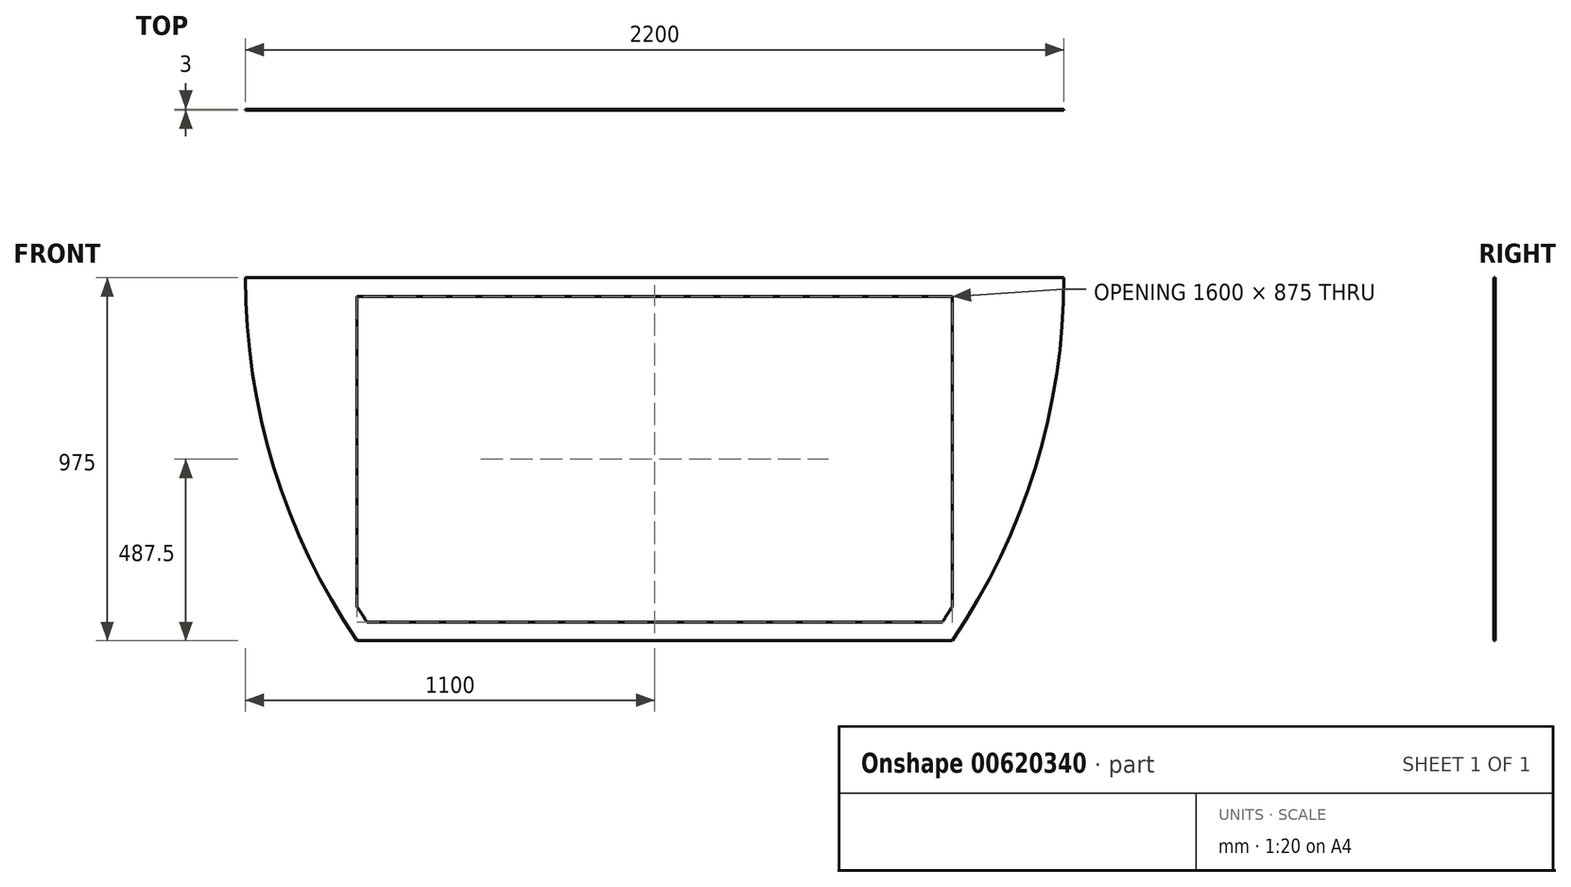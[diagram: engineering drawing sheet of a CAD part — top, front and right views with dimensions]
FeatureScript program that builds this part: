
annotation { "Feature Type Name" : "Feature", "Feature Type Description" : "" }
export const myFeature = defineFeature(function(context is Context, id is Id, definition is map)
    precondition{}
    {
        {
            var Q0;
            Q0=qCreatedBy(makeId("Front.planeOp"),FACE);
            var sketch = newSketch(context, id + "F0", { "sketchPlane" : qUnion([Q0])});
            skLineSegment(sketch, "E0.bottom", {"start": v(-800, 1950) * mm, "end": v(800, 1950) * mm});
            skLineSegment(sketch, "E0.top", {"start": v(-800, 0) * mm, "end": v(800, 0) * mm});
            skLineSegment(sketch, "E0.left", {"start": v(-800, 1950) * mm, "end": v(-800, 0) * mm});
            skLineSegment(sketch, "E0.right", {"start": v(800, 1950) * mm, "end": v(800, 0) * mm});
            skArc(sketch, "E1", {"start": v(800, 0) * mm, "mid": v(1100, 975) * mm, "end": v(800, 1950) * mm});
            skArc(sketch, "E2", {"start": v(-800, 1950) * mm, "mid": v(-1100, 975) * mm, "end": v(-800, 0) * mm});
            skArc(sketch, "E3", {"start": v(-804.9, 1850) * mm, "mid": v(-1049.74, 945.42) * mm, "end": v(-773.28, 50) * mm});
            skArc(sketch, "E4", {"start": v(773.28, 50) * mm, "mid": v(1049.74, 945.42) * mm, "end": v(804.9, 1850) * mm});
            skLineSegment(sketch, "E5", {"start": v(-1050, 975) * mm, "end": v(1050, 975) * mm});
            skPoint(sketch, "E5.startSnap0", {"position": v(-1100, 975) * mm});
            skLineSegment(sketch, "E6", {"start": v(-804.9, 1850) * mm, "end": v(804.9, 1850) * mm});
            skLineSegment(sketch, "E7", {"start": v(-773.28, 50) * mm, "end": v(773.28, 50) * mm});
            skLineSegment(sketch, "E8", {"start": v(0, 1950) * mm, "end": v(0, 975) * mm});
            skLineSegment(sketch, "E9", {"start": v(-25, 1850) * mm, "end": v(-25, 975) * mm});
            skLineSegment(sketch, "E10", {"start": v(-25, 975) * mm, "end": v(25, 975) * mm});
            skLineSegment(sketch, "E11", {"start": v(25, 975) * mm, "end": v(25, 1850) * mm});
            skLineSegment(sketch, "E12", {"start": v(-1099.28, 925) * mm, "end": v(1099.28, 925) * mm});
            skLineSegment(sketch, "E13", {"start": v(-25, 975) * mm, "end": v(-25, 925) * mm});
            skLineSegment(sketch, "E14", {"start": v(25, 975) * mm, "end": v(25, 925) * mm});
            skLineSegment(sketch, "E15", {"start": v(-750, 0) * mm, "end": v(-750, 50) * mm});
            skLineSegment(sketch, "E16", {"start": v(-750, 50) * mm, "end": v(-650, 50) * mm});
            skLineSegment(sketch, "E17", {"start": v(-650, 50) * mm, "end": v(-650, 0) * mm});
            skLineSegment(sketch, "E18", {"start": v(-50, 0) * mm, "end": v(-50, 50) * mm});
            skLineSegment(sketch, "E19", {"start": v(-50, 50) * mm, "end": v(50, 50) * mm});
            skLineSegment(sketch, "E20", {"start": v(50, 50) * mm, "end": v(50, 0) * mm});
            skLineSegment(sketch, "E21", {"start": v(650, 0) * mm, "end": v(650, 50) * mm});
            skLineSegment(sketch, "E22", {"start": v(650, 50) * mm, "end": v(750, 50) * mm});
            skLineSegment(sketch, "E23", {"start": v(750, 50) * mm, "end": v(750, 0) * mm});
            skLineSegment(sketch, "E24", {"start": v(0, 50) * mm, "end": v(0, 0) * mm});
            skLineSegment(sketch, "E25", {"start": v(-800, 1900) * mm, "end": v(800, 1900) * mm});
            skLineSegment(sketch, "E26", {"start": v(-1050, 975) * mm, "end": v(-1100, 975) * mm});
            skLineSegment(sketch, "E27", {"start": v(1050, 975) * mm, "end": v(1100, 975) * mm});
            skSolve(sketch);
        }
        {
            var Q0;
            {var subQ3=sQuery(id+"F0.wireOp",EDGE,"E15");Q0=makeQuery(id+"F0.imprint","IMPRINT",FACE,{"disambiguationData":[TD([[makeQuery(id+"F0.imprint","IMPRINT",EDGE,{"derivedFrom":subQ3}),1.0]])]});}
            var Q1;
            {var subQ0=sQuery(id+"F0.wireOp",EDGE,"E15");Q1=makeQuery(id+"F0.imprint","IMPRINT",FACE,{"disambiguationData":[TD([[makeQuery(id+"F0.imprint","IMPRINT",EDGE,{"derivedFrom":subQ0}),-1.0]])]});}
            var Q2;
            {var subQ0=sQuery(id+"F0.wireOp",EDGE,"E17");Q2=makeQuery(id+"F0.imprint","IMPRINT",FACE,{"disambiguationData":[TD([[makeQuery(id+"F0.imprint","IMPRINT",EDGE,{"derivedFrom":subQ0}),1.0]])]});}
            var Q3;
            {var subQ0=sQuery(id+"F0.wireOp",EDGE,"E18");Q3=makeQuery(id+"F0.imprint","IMPRINT",FACE,{"disambiguationData":[TD([[makeQuery(id+"F0.imprint","IMPRINT",EDGE,{"derivedFrom":subQ0}),-1.0]])]});}
            var Q4;
            {var subQ0=sQuery(id+"F0.wireOp",EDGE,"E20");Q4=makeQuery(id+"F0.imprint","IMPRINT",FACE,{"disambiguationData":[TD([[makeQuery(id+"F0.imprint","IMPRINT",EDGE,{"derivedFrom":subQ0}),-1.0]])]});}
            var Q5;
            {var subQ0=sQuery(id+"F0.wireOp",EDGE,"E20");Q5=makeQuery(id+"F0.imprint","IMPRINT",FACE,{"disambiguationData":[TD([[makeQuery(id+"F0.imprint","IMPRINT",EDGE,{"derivedFrom":subQ0}),1.0]])]});}
            var Q6;
            {var subQ0=sQuery(id+"F0.wireOp",EDGE,"E21");Q6=makeQuery(id+"F0.imprint","IMPRINT",FACE,{"disambiguationData":[TD([[makeQuery(id+"F0.imprint","IMPRINT",EDGE,{"derivedFrom":subQ0}),-1.0]])]});}
            var Q7;
            {var subQ7=sQuery(id+"F0.wireOp",EDGE,"E23");Q7=makeQuery(id+"F0.imprint","IMPRINT",FACE,{"disambiguationData":[TD([[makeQuery(id+"F0.imprint","IMPRINT",EDGE,{"derivedFrom":subQ7}),1.0]])]});}
            var Q8;
            {var subQ1=sQuery(id+"F0.wireOp",EDGE,"E0.left");var subQ3=sQuery(id+"F0.wireOp",EDGE,"E3");var subQ4=makeQuery(id+"F0.imprint","INTERSECT",VERTEX,{"derivedFrom":[subQ1,subQ3]});Q8=makeQuery(id+"F0.imprint","IMPRINT",FACE,{"disambiguationData":[TD([[makeQuery(id+"F0.imprint","IMPRINT",EDGE,{"disambiguationData":[TD([[subQ4,1.0]])],"derivedFrom":subQ3}),-1.0]])]});}
            var Q9;
            {var subQ1=sQuery(id+"F0.wireOp",EDGE,"E0.right");var subQ3=sQuery(id+"F0.wireOp",EDGE,"E4");var subQ4=makeQuery(id+"F0.imprint","INTERSECT",VERTEX,{"derivedFrom":[subQ1,subQ3]});Q9=makeQuery(id+"F0.imprint","IMPRINT",FACE,{"disambiguationData":[TD([[makeQuery(id+"F0.imprint","IMPRINT",EDGE,{"disambiguationData":[TD([[subQ4,-1.0]])],"derivedFrom":subQ3}),-1.0]])]});}
            var Q10;
            {var subQ3=sQuery(id+"F0.wireOp",EDGE,"E27");Q10=makeQuery(id+"F0.imprint","IMPRINT",FACE,{"disambiguationData":[TD([[makeQuery(id+"F0.imprint","IMPRINT",EDGE,{"derivedFrom":subQ3}),-1.0]])]});}
            var Q11;
            {var subQ3=sQuery(id+"F0.wireOp",EDGE,"E26");Q11=makeQuery(id+"F0.imprint","IMPRINT",FACE,{"disambiguationData":[TD([[makeQuery(id+"F0.imprint","IMPRINT",EDGE,{"derivedFrom":subQ3}),1.0]])]});}
            var Q12;
            {var subQ0=sQuery(id+"F0.wireOp",EDGE,"E12");var subQ1=sQuery(id+"F0.wireOp",EDGE,"E0.left");var subQ2=makeQuery(id+"F0.imprint","INTERSECT",VERTEX,{"derivedFrom":[subQ1,subQ0]});Q12=makeQuery(id+"F0.imprint","IMPRINT",FACE,{"disambiguationData":[TD([[makeQuery(id+"F0.imprint","IMPRINT",EDGE,{"disambiguationData":[TD([[subQ2,-1.0]])],"derivedFrom":subQ1}),-1.0]])]});}
            var Q13;
            {var subQ15=sQuery(id+"F0.wireOp",EDGE,"E16");Q13=makeQuery(id+"F0.imprint","IMPRINT",FACE,{"disambiguationData":[TD([[makeQuery(id+"F0.imprint","IMPRINT",EDGE,{"derivedFrom":subQ15}),1.0]])]});}
            var Q14;
            {var subQ0=sQuery(id+"F0.wireOp",EDGE,"E12");var subQ1=sQuery(id+"F0.wireOp",EDGE,"E0.right");var subQ2=makeQuery(id+"F0.imprint","INTERSECT",VERTEX,{"derivedFrom":[subQ1,subQ0]});Q14=makeQuery(id+"F0.imprint","IMPRINT",FACE,{"disambiguationData":[TD([[makeQuery(id+"F0.imprint","IMPRINT",EDGE,{"disambiguationData":[TD([[subQ2,-1.0]])],"derivedFrom":subQ1}),1.0]])]});}
            var Q15;
            {var subQ0=sQuery(id+"F0.wireOp",EDGE,"E5");var subQ1=sQuery(id+"F0.wireOp",EDGE,"E0.right");var subQ2=makeQuery(id+"F0.imprint","INTERSECT",VERTEX,{"derivedFrom":[subQ1,subQ0]});Q15=makeQuery(id+"F0.imprint","IMPRINT",FACE,{"disambiguationData":[TD([[makeQuery(id+"F0.imprint","IMPRINT",EDGE,{"disambiguationData":[TD([[subQ2,-1.0]])],"derivedFrom":subQ1}),1.0]])]});}
            var Q16;
            {var subQ5=sQuery(id+"F0.wireOp",EDGE,"E14");Q16=makeQuery(id+"F0.imprint","IMPRINT",FACE,{"disambiguationData":[TD([[makeQuery(id+"F0.imprint","IMPRINT",EDGE,{"derivedFrom":subQ5}),1.0]])]});}
            var Q17;
            {var subQ0=sQuery(id+"F0.wireOp",EDGE,"E13");Q17=makeQuery(id+"F0.imprint","IMPRINT",FACE,{"disambiguationData":[TD([[makeQuery(id+"F0.imprint","IMPRINT",EDGE,{"derivedFrom":subQ0}),1.0]])]});}
            var Q18;
            {var subQ5=sQuery(id+"F0.wireOp",EDGE,"E13");Q18=makeQuery(id+"F0.imprint","IMPRINT",FACE,{"disambiguationData":[TD([[makeQuery(id+"F0.imprint","IMPRINT",EDGE,{"derivedFrom":subQ5}),-1.0]])]});}
            var Q19;
            {var subQ0=sQuery(id+"F0.wireOp",EDGE,"E5");var subQ1=sQuery(id+"F0.wireOp",EDGE,"E0.left");var subQ2=makeQuery(id+"F0.imprint","INTERSECT",VERTEX,{"derivedFrom":[subQ1,subQ0]});Q19=makeQuery(id+"F0.imprint","IMPRINT",FACE,{"disambiguationData":[TD([[makeQuery(id+"F0.imprint","IMPRINT",EDGE,{"disambiguationData":[TD([[subQ2,-1.0]])],"derivedFrom":subQ1}),-1.0]])]});}
            extrude(context, id + "F1", {"entities" : qUnion([Q0, Q1, Q2, Q3, Q4, Q5, Q6, Q7, Q8, Q9, Q10, Q11, Q12, Q13, Q14, Q15, Q16, Q17, Q18, Q19]), "depth" : 3 * mm, "offsetDistance" : 25 * mm});
        }
    });
